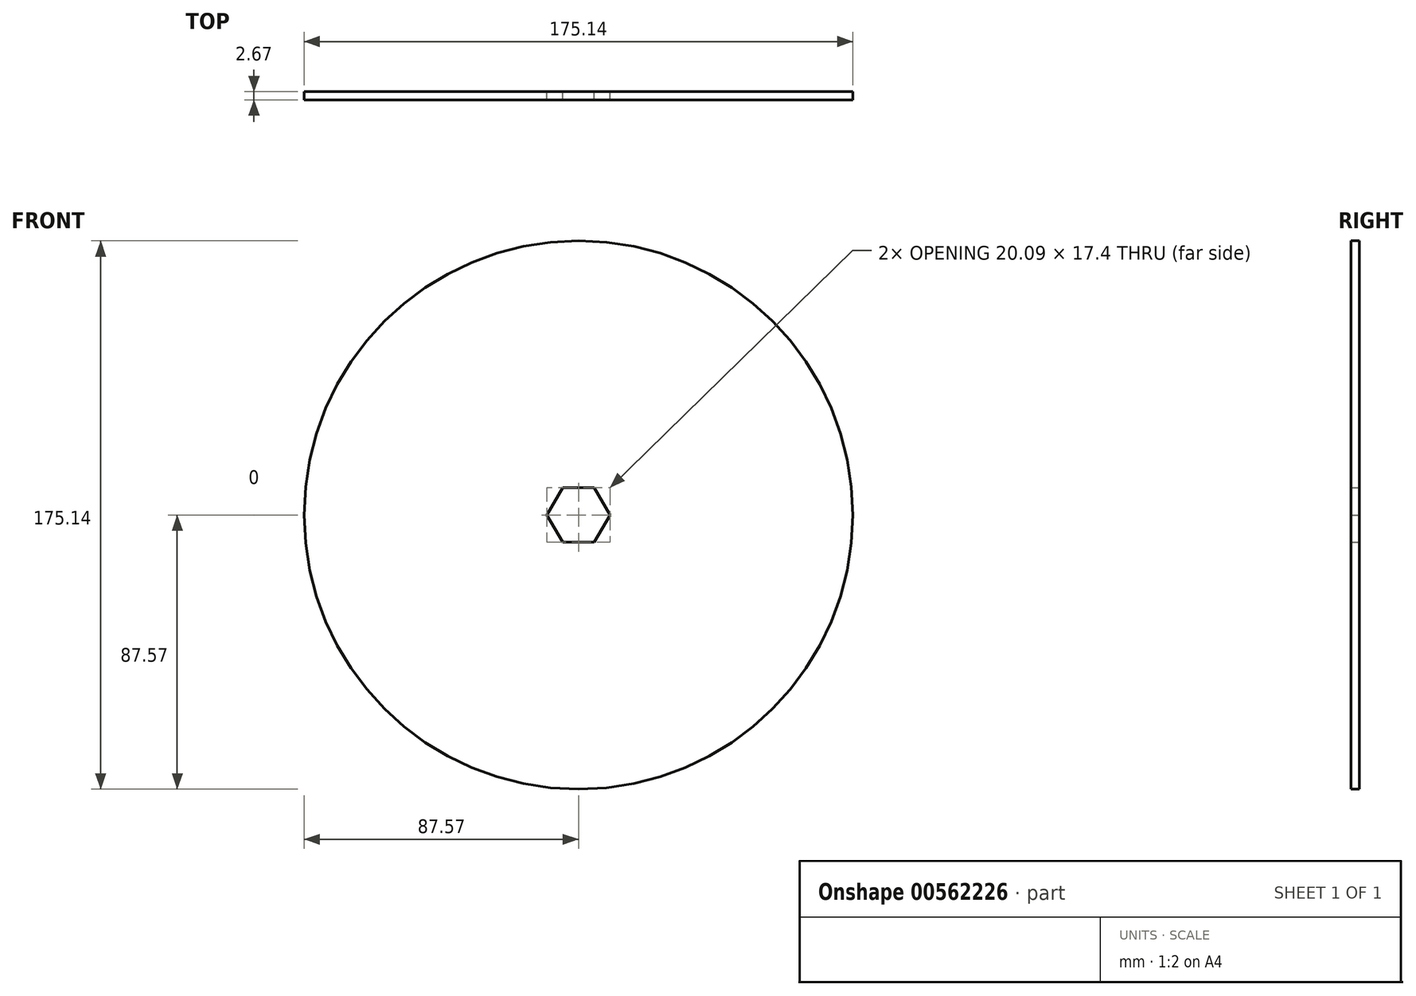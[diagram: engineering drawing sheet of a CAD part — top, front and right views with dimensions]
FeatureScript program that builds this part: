
annotation { "Feature Type Name" : "Feature", "Feature Type Description" : "" }
export const myFeature = defineFeature(function(context is Context, id is Id, definition is map)
    precondition{}
    {
        {
            var Q0;
            Q0=qCreatedBy(makeId("Front.planeOp"),FACE);
            var sketch = newSketch(context, id + "F0", { "sketchPlane" : qUnion([Q0])});
            skCircle(sketch, "E0", {"center": v(0, 0) * mm, "radius": 87.57 * mm});
            skCircle(sketch, "E1.cCircle", {"center": v(0, 0) * mm, "radius": 8.7 * mm, "construction": true});
            skLineSegment(sketch, "E1.0", {"start": v(5.02, -8.7) * mm, "end": v(-5.02, -8.7) * mm});
            skLineSegment(sketch, "E1.1", {"start": v(-5.02, -8.7) * mm, "end": v(-10.05, 0) * mm});
            skLineSegment(sketch, "E1.2", {"start": v(-10.05, 0) * mm, "end": v(-5.02, 8.7) * mm});
            skLineSegment(sketch, "E1.3", {"start": v(-5.02, 8.7) * mm, "end": v(5.02, 8.7) * mm});
            skLineSegment(sketch, "E1.4", {"start": v(5.02, 8.7) * mm, "end": v(10.05, 0) * mm});
            skLineSegment(sketch, "E1.5", {"start": v(10.05, 0) * mm, "end": v(5.02, -8.7) * mm});
            skPoint(sketch, "E1.0.midPoint", {"position": v(0, -8.7) * mm});
            skSolve(sketch);
        }
        {
            var Q0;
            Q0 = qSketchRegion(id + "F0", true);
            extrude(context, id + "F1", {"entities" : qUnion([Q0]), "depth" : 2.67 * mm, "offsetDistance" : 25.4 * mm});
        }
    });
